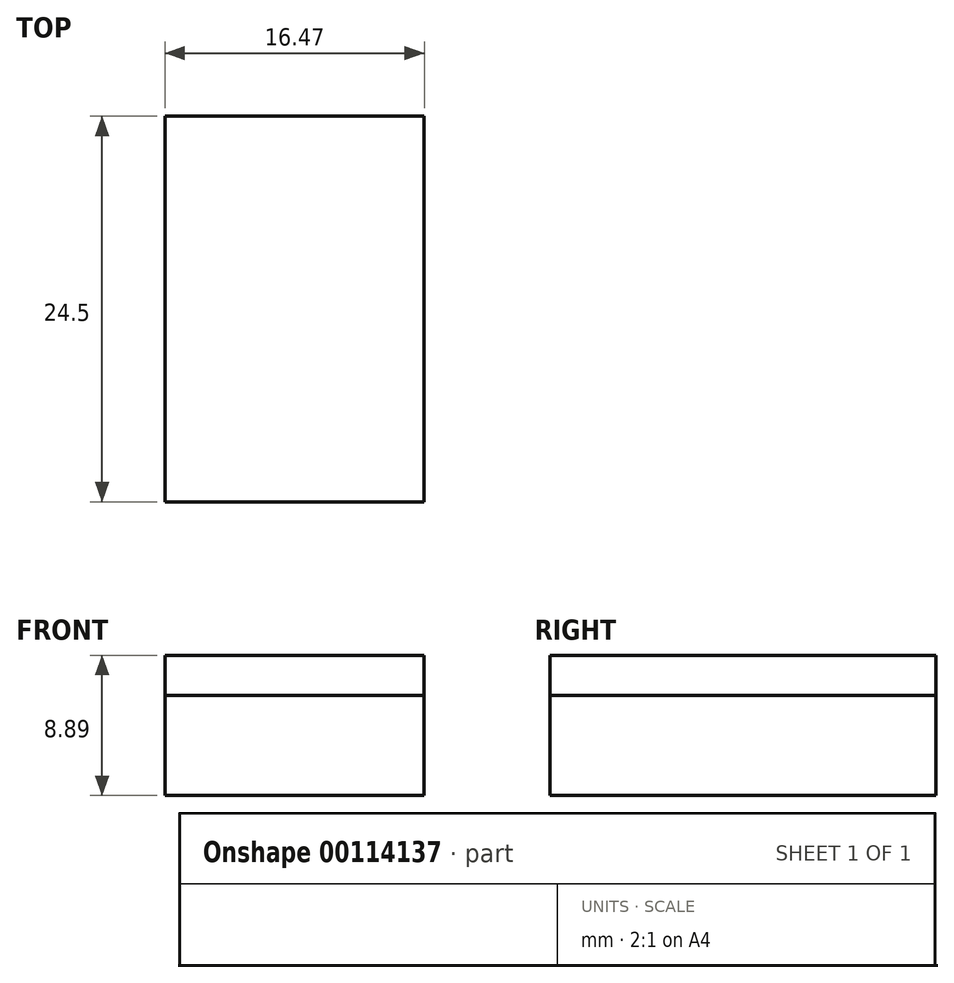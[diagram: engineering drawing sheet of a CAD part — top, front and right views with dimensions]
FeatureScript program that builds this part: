
annotation { "Feature Type Name" : "Feature", "Feature Type Description" : "" }
export const myFeature = defineFeature(function(context is Context, id is Id, definition is map)
    precondition{}
    {
        {
            var Q0;
            Q0=qCreatedBy(makeId("Top.planeOp"),FACE);
            var sketch = newSketch(context, id + "F0", { "sketchPlane" : qUnion([Q0])});
            skLineSegment(sketch, "E0.bottom", {"start": v(-7.99, 12.48) * mm, "end": v(8.48, 12.48) * mm});
            skLineSegment(sketch, "E0.top", {"start": v(-7.99, -12.02) * mm, "end": v(8.48, -12.02) * mm});
            skLineSegment(sketch, "E0.left", {"start": v(-7.99, 12.48) * mm, "end": v(-7.99, -12.02) * mm});
            skLineSegment(sketch, "E0.right", {"start": v(8.48, 12.48) * mm, "end": v(8.48, -12.02) * mm});
            skSolve(sketch);
        }
        {
            var Q0;
            Q0=makeQuery(id+"F0.imprint","IMPRINT",FACE,{"disambiguationData":[TD([[makeQuery(id+"F0.imprint","IMPRINT",EDGE,{"derivedFrom":sQuery(id+"F0.wireOp",EDGE,"E0.bottom")}),-1.0]])]});
            extrude(context, id + "F1", {"entities" : qUnion([Q0]), "depth" : 6.35 * mm});
        }
        {
            var Q0;
            Q0=makeQuery(id+"F1.opExtrude","CAP_FACE",FACE,{"disambiguationData":[OSD([sQuery(id+"F0.wireOp",EDGE,"E0.bottom"),sQuery(id+"F0.wireOp",EDGE,"E0.top"),sQuery(id+"F0.wireOp",EDGE,"E0.left"),sQuery(id+"F0.wireOp",EDGE,"E0.right")])],"isStart":false});
            var sketch = newSketch(context, id + "F2", { "sketchPlane" : qUnion([Q0])});
            skLineSegment(sketch, "E1.bottom", {"start": v(-7.99, 12.48) * mm, "end": v(8.48, 12.48) * mm});
            skLineSegment(sketch, "E1.top", {"start": v(-7.99, -12.02) * mm, "end": v(8.48, -12.02) * mm});
            skLineSegment(sketch, "E1.left", {"start": v(-7.99, 12.48) * mm, "end": v(-7.99, -12.02) * mm});
            skLineSegment(sketch, "E1.right", {"start": v(8.48, 12.48) * mm, "end": v(8.48, -12.02) * mm});
            skSolve(sketch);
        }
        {
            var Q0;
            Q0 = qSketchRegion(id + "F2", true);
            extrude(context, id + "F3", {"entities" : qUnion([Q0]), "depth" : 2.54 * mm});
        }
    });
